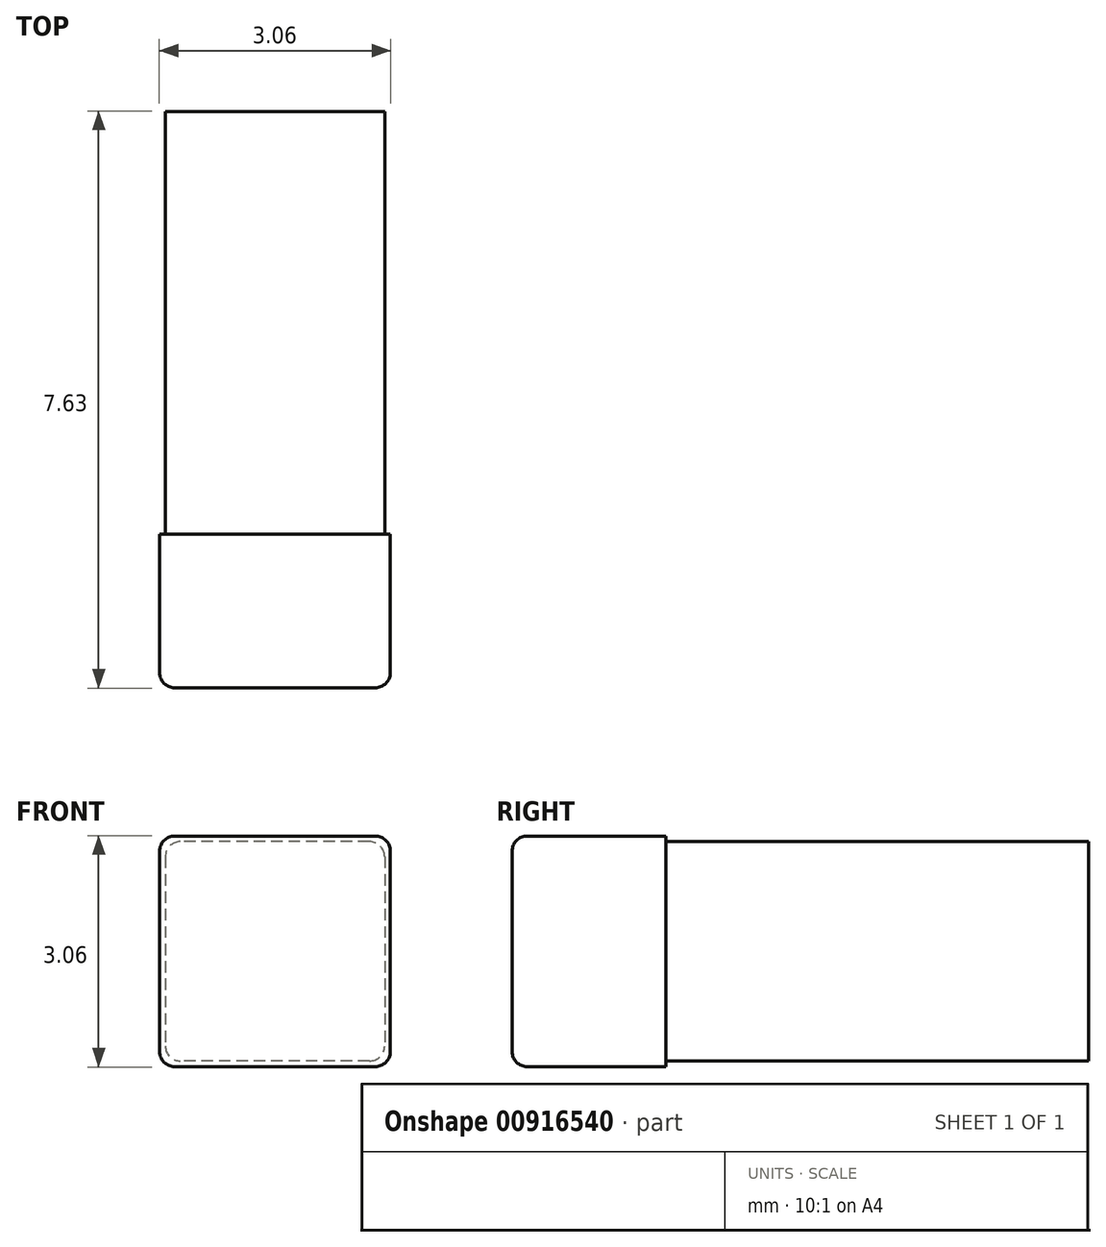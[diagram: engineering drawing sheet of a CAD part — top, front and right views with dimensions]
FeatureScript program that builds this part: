
annotation { "Feature Type Name" : "Feature", "Feature Type Description" : "" }
export const myFeature = defineFeature(function(context is Context, id is Id, definition is map)
    precondition{}
    {
        {
            assignVariable(context, id + "F0", {"name" : "CapLength", "anyValue" : 2.03});
        }
        {
            assignVariable(context, id + "F1", {"name" : "Length", "anyValue" : 9.65});
        }
        {
            var Q0;
            Q0=qCreatedBy(makeId("Front.planeOp"),FACE);
            var sketch = newSketch(context, id + "F2", { "sketchPlane" : qUnion([Q0])});
            skLineSegment(sketch, "E0.bottom", {"start": v(1.45, 1.45) * mm, "end": v(-1.45, 1.45) * mm});
            skLineSegment(sketch, "E0.top", {"start": v(1.45, -1.45) * mm, "end": v(-1.45, -1.45) * mm});
            skLineSegment(sketch, "E0.left", {"start": v(1.45, 1.45) * mm, "end": v(1.45, -1.45) * mm});
            skLineSegment(sketch, "E0.right", {"start": v(-1.45, 1.45) * mm, "end": v(-1.45, -1.45) * mm});
            skPoint(sketch, "E0.middle", {"position": v(0, 0) * mm});
            skSolve(sketch);
        }
        {
            var Q0;
            Q0 = qSketchRegion(id + "F2", true);
            extrude(context, id + "F3", {"entities" : qUnion([Q0]), "depth" : (getVariable(context, 'Length') - (2 * getVariable(context, 'CapLength'))) * mm, "offsetDistance" : 25 * mm, "symmetric" : true});
        }
        {
            var Q0;
            Q0=makeQuery(id+"F3.opExtrude","CAP_FACE",FACE,{"disambiguationData":[OSD([sQuery(id+"F2.wireOp",EDGE,"E0.bottom"),sQuery(id+"F2.wireOp",EDGE,"E0.top"),sQuery(id+"F2.wireOp",EDGE,"E0.left"),sQuery(id+"F2.wireOp",EDGE,"E0.right")])],"isStart":false});
            var sketch = newSketch(context, id + "F4", { "sketchPlane" : qUnion([Q0])});
            skLineSegment(sketch, "E1.bottom", {"start": v(1.53, 1.52) * mm, "end": v(-1.52, 1.52) * mm});
            skLineSegment(sketch, "E1.top", {"start": v(1.52, -1.52) * mm, "end": v(-1.52, -1.52) * mm});
            skLineSegment(sketch, "E1.left", {"start": v(1.53, 1.52) * mm, "end": v(1.53, -1.52) * mm});
            skLineSegment(sketch, "E1.right", {"start": v(-1.52, 1.52) * mm, "end": v(-1.52, -1.52) * mm});
            skPoint(sketch, "E1.middle", {"position": v(0, 0) * mm});
            skSolve(sketch);
        }
        {
            var Q0;
            Q0 = qSketchRegion(id + "F4", true);
            extrude(context, id + "F5", {"entities" : qUnion([Q0]), "depth" : (getVariable(context, 'CapLength')) * mm, "offsetDistance" : 25 * mm});
        }
        {
            var Q0;
            Q0=makeQuery(id+"F5.opExtrude","CAP_FACE",FACE,{"disambiguationData":[OSD([sQuery(id+"F4.wireOp",EDGE,"E1.bottom"),sQuery(id+"F4.wireOp",EDGE,"E1.top"),sQuery(id+"F4.wireOp",EDGE,"E1.left"),sQuery(id+"F4.wireOp",EDGE,"E1.right")])],"isStart":false});
            var Q1;
            Q1=makeQuery(id+"FsKa9ejSSYPuka9_1.1.F5.opExtrude","CAP_FACE",FACE,{"disambiguationData":[OSD([sQuery(id+"F4.wireOp",EDGE,"E1.bottom"),sQuery(id+"F4.wireOp",EDGE,"E1.top"),sQuery(id+"F4.wireOp",EDGE,"E1.left"),sQuery(id+"F4.wireOp",EDGE,"E1.right")])],"isStart":false});
            var Q2;
            Q2=makeQuery(id+"FsKa9ejSSYPuka9_1.1.F5.opExtrude","SWEPT_EDGE",EDGE,{"disambiguationData":[OSD([sQuery(id+"F4.wireOp",EDGE,"E1.bottom"),sQuery(id+"F4.wireOp",EDGE,"E1.left")])]});
            var Q3;
            Q3=makeQuery(id+"FsKa9ejSSYPuka9_1.1.F5.opExtrude","SWEPT_EDGE",EDGE,{"disambiguationData":[OSD([sQuery(id+"F4.wireOp",EDGE,"E1.top"),sQuery(id+"F4.wireOp",EDGE,"E1.left")])]});
            var Q4;
            Q4=makeQuery(id+"FsKa9ejSSYPuka9_1.1.F5.opExtrude","SWEPT_EDGE",EDGE,{"disambiguationData":[OSD([sQuery(id+"F4.wireOp",EDGE,"E1.top"),sQuery(id+"F4.wireOp",EDGE,"E1.right")])]});
            var Q5;
            Q5=makeQuery(id+"FsKa9ejSSYPuka9_1.1.F5.opExtrude","SWEPT_EDGE",EDGE,{"disambiguationData":[OSD([sQuery(id+"F4.wireOp",EDGE,"E1.bottom"),sQuery(id+"F4.wireOp",EDGE,"E1.right")])]});
            var Q6;
            Q6=makeQuery(id+"F5.opExtrude","SWEPT_EDGE",EDGE,{"disambiguationData":[OSD([sQuery(id+"F4.wireOp",EDGE,"E1.top"),sQuery(id+"F4.wireOp",EDGE,"E1.left")])]});
            var Q7;
            Q7=makeQuery(id+"F5.opExtrude","SWEPT_EDGE",EDGE,{"disambiguationData":[OSD([sQuery(id+"F4.wireOp",EDGE,"E1.top"),sQuery(id+"F4.wireOp",EDGE,"E1.right")])]});
            var Q8;
            Q8=makeQuery(id+"F5.opExtrude","SWEPT_EDGE",EDGE,{"disambiguationData":[OSD([sQuery(id+"F4.wireOp",EDGE,"E1.bottom"),sQuery(id+"F4.wireOp",EDGE,"E1.left")])]});
            var Q9;
            Q9=makeQuery(id+"F5.opExtrude","SWEPT_EDGE",EDGE,{"disambiguationData":[OSD([sQuery(id+"F4.wireOp",EDGE,"E1.bottom"),sQuery(id+"F4.wireOp",EDGE,"E1.right")])]});
            fillet(context, id + "F6", {"entities" : qUnion([Q0, Q1, Q2, Q3, Q4, Q5, Q6, Q7, Q8, Q9]), "radius" : .2 * mm, "tangentPropagation" : true, "allowEdgeOverflow" : false});
        }
        {
            var Q0;
            Q0=makeQuery(id+"F3.opExtrude","SWEPT_EDGE",EDGE,{"disambiguationData":[OSD([sQuery(id+"F2.wireOp",EDGE,"E0.bottom"),sQuery(id+"F2.wireOp",EDGE,"E0.left")])]});
            var Q1;
            Q1=makeQuery(id+"F3.opExtrude","SWEPT_EDGE",EDGE,{"disambiguationData":[OSD([sQuery(id+"F2.wireOp",EDGE,"E0.top"),sQuery(id+"F2.wireOp",EDGE,"E0.left")])]});
            var Q2;
            Q2=makeQuery(id+"F3.opExtrude","SWEPT_EDGE",EDGE,{"disambiguationData":[OSD([sQuery(id+"F2.wireOp",EDGE,"E0.bottom"),sQuery(id+"F2.wireOp",EDGE,"E0.right")])]});
            var Q3;
            Q3=makeQuery(id+"F3.opExtrude","SWEPT_EDGE",EDGE,{"disambiguationData":[OSD([sQuery(id+"F2.wireOp",EDGE,"E0.top"),sQuery(id+"F2.wireOp",EDGE,"E0.right")])]});
            fillet(context, id + "F7", {"entities" : qUnion([Q0, Q1, Q2, Q3]), "radius" : .2 * mm, "tangentPropagation" : true, "allowEdgeOverflow" : false});
        }
    });
